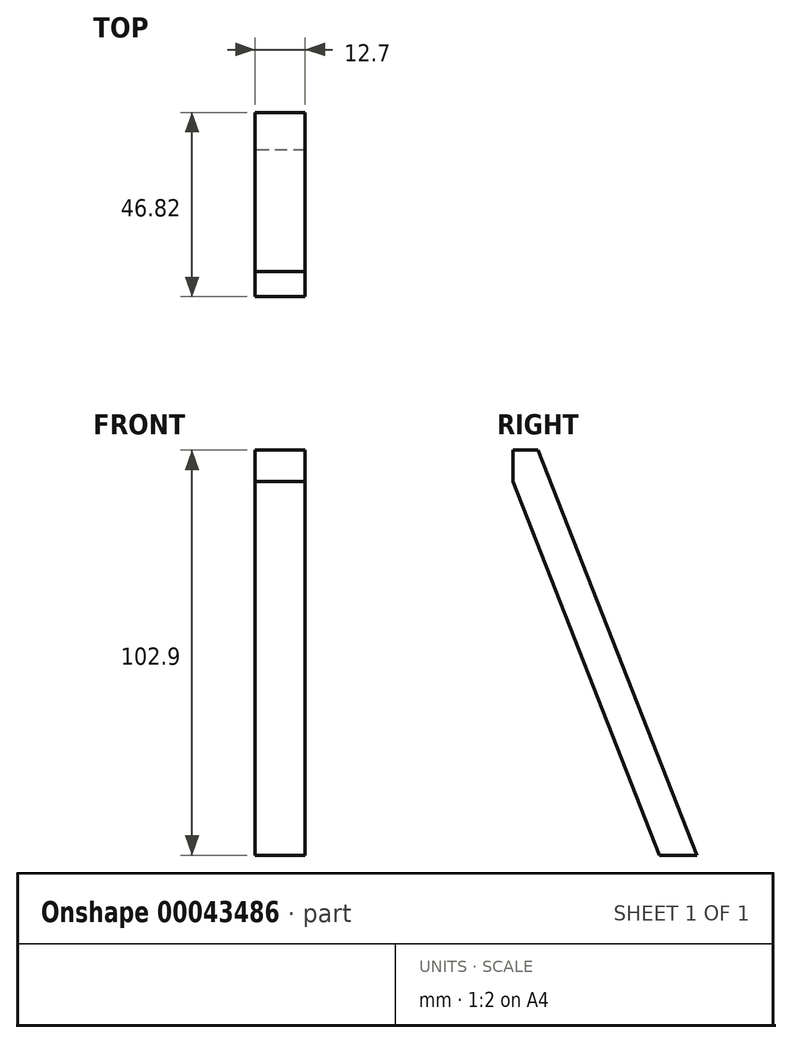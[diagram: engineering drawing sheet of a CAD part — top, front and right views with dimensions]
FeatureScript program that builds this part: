
annotation { "Feature Type Name" : "Feature", "Feature Type Description" : "" }
export const myFeature = defineFeature(function(context is Context, id is Id, definition is map)
    precondition{}
    {
        {
            var Q0;
            Q0=qCreatedBy(makeId("Right.planeOp"),FACE);
            var sketch = newSketch(context, id + "F0", { "sketchPlane" : qUnion([Q0])});
            skLineSegment(sketch, "E0", {"start": v(0, 47.6) * mm, "end": v(0, 39.62) * mm});
            skLineSegment(sketch, "E1", {"start": v(0, 39.62) * mm, "end": v(37.3, -55.31) * mm});
            skLineSegment(sketch, "E2", {"start": v(37.3, -55.31) * mm, "end": v(46.82, -55.31) * mm});
            skLineSegment(sketch, "E3", {"start": v(46.82, -55.31) * mm, "end": v(6.38, 47.6) * mm});
            skLineSegment(sketch, "E4", {"start": v(6.38, 47.6) * mm, "end": v(0, 47.6) * mm});
            skSolve(sketch);
        }
        {
            var Q0;
            Q0 = qSketchRegion(id + "F0", true);
            extrude(context, id + "F1", {"entities" : qUnion([Q0]), "depth" : 12.7 * mm});
        }
    });
